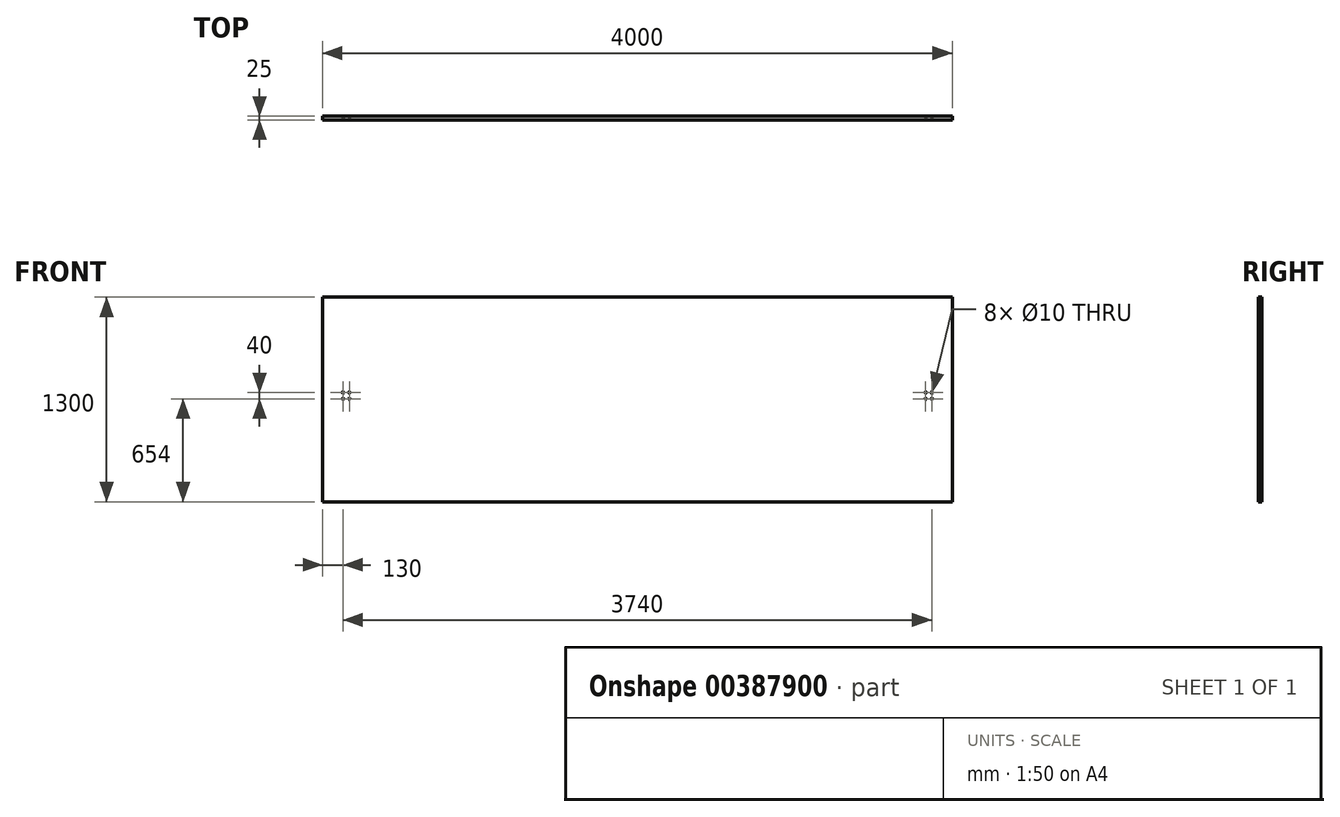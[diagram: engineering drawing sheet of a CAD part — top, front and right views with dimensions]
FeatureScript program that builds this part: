
annotation { "Feature Type Name" : "Feature", "Feature Type Description" : "" }
export const myFeature = defineFeature(function(context is Context, id is Id, definition is map)
    precondition{}
    {
        {
            var Q0;
            Q0=qCreatedBy(makeId("Front.planeOp"),FACE);
            var sketch = newSketch(context, id + "F0", { "sketchPlane" : qUnion([Q0])});
            skLineSegment(sketch, "E0.bottom", {"start": v(-2000, 650) * mm, "end": v(2000, 650) * mm});
            skLineSegment(sketch, "E0.top", {"start": v(-2000, -650) * mm, "end": v(2000, -650) * mm});
            skLineSegment(sketch, "E0.left", {"start": v(-2000, 650) * mm, "end": v(-2000, -650) * mm});
            skLineSegment(sketch, "E0.right", {"start": v(2000, 650) * mm, "end": v(2000, -650) * mm});
            skPoint(sketch, "E0.middle", {"position": v(0, 0) * mm});
            skSolve(sketch);
        }
        {
            var Q0;
            Q0 = qSketchRegion(id + "F0", true);
            extrude(context, id + "F1", {"entities" : qUnion([Q0]), "depth" : 25 * mm});
        }
        {
            var Q0;
            Q0=makeQuery(id+"F1.opExtrude","CAP_FACE",FACE,{"disambiguationData":[OSD([sQuery(id+"F0.wireOp",EDGE,"E0.bottom"),sQuery(id+"F0.wireOp",EDGE,"E0.top"),sQuery(id+"F0.wireOp",EDGE,"E0.left"),sQuery(id+"F0.wireOp",EDGE,"E0.right")])],"isStart":false});
            var sketch = newSketch(context, id + "F2", { "sketchPlane" : qUnion([Q0])});
            skLineSegment(sketch, "E1", {"start": v(-2000, 650) * mm, "end": v(-1850, 650) * mm});
            skLineSegment(sketch, "E2", {"start": v(-1850, 650) * mm, "end": v(-1850, 24) * mm});
            skLineSegment(sketch, "E3.bottom", {"start": v(-1870, 44) * mm, "end": v(-1830, 44) * mm});
            skLineSegment(sketch, "E3.top", {"start": v(-1870, 4) * mm, "end": v(-1830, 4) * mm});
            skLineSegment(sketch, "E3.left", {"start": v(-1870, 44) * mm, "end": v(-1870, 4) * mm});
            skLineSegment(sketch, "E3.right", {"start": v(-1830, 44) * mm, "end": v(-1830, 4) * mm});
            skPoint(sketch, "E3.middle", {"position": v(-1850, 24) * mm});
            skLineSegment(sketch, "E4", {"start": v(2000, 650) * mm, "end": v(1850, 650) * mm});
            skLineSegment(sketch, "E5", {"start": v(1850, 650) * mm, "end": v(1850, 24) * mm});
            skLineSegment(sketch, "E6.bottom", {"start": v(1830, 44) * mm, "end": v(1870, 44) * mm});
            skLineSegment(sketch, "E6.top", {"start": v(1830, 4) * mm, "end": v(1870, 4) * mm});
            skLineSegment(sketch, "E6.left", {"start": v(1830, 44) * mm, "end": v(1830, 4) * mm});
            skLineSegment(sketch, "E6.right", {"start": v(1870, 44) * mm, "end": v(1870, 4) * mm});
            skPoint(sketch, "E6.middle", {"position": v(1850, 24) * mm});
            skSolve(sketch);
        }
        {
            var Q0;
            Q0=sQuery(id+"F2.wireOp",VERTEX,"E3.bottom.start");
            var Q1;
            Q1=sQuery(id+"F2.wireOp",VERTEX,"E3.bottom.end");
            var Q2;
            Q2=sQuery(id+"F2.wireOp",VERTEX,"E3.right.end");
            var Q3;
            Q3=sQuery(id+"F2.wireOp",VERTEX,"E3.top.start");
            var Q4;
            Q4=makeQuery(id+"F1.opExtrude","SWEPT_BODY",BODY,{"disambiguationData":[OSD([sQuery(id+"F0.wireOp",EDGE,"E0.bottom"),sQuery(id+"F0.wireOp",EDGE,"E0.top"),sQuery(id+"F0.wireOp",EDGE,"E0.left"),sQuery(id+"F0.wireOp",EDGE,"E0.right")])]});
            hole(context, id + "F3", {"style" : HoleStyle.SIMPLE, "endStyle" : HoleEndStyle.THROUGH, "holeDiameter" : 10 * mm, "isTappedThrough" : true, "tappedDepth" : 12 * mm, "tapClearance" : 3, "locations" : qUnion([Q0, Q1, Q2, Q3]), "scope" : qUnion([Q4])});
        }
        {
            var Q0;
            Q0=sQuery(id+"F2.wireOp",VERTEX,"E6.bottom.start");
            var Q1;
            Q1=sQuery(id+"F2.wireOp",VERTEX,"E6.bottom.end");
            var Q2;
            Q2=sQuery(id+"F2.wireOp",VERTEX,"E6.top.end");
            var Q3;
            Q3=sQuery(id+"F2.wireOp",VERTEX,"E6.top.start");
            var Q4;
            Q4=makeQuery(id+"F1.opExtrude","SWEPT_BODY",BODY,{"disambiguationData":[OSD([sQuery(id+"F0.wireOp",EDGE,"E0.bottom"),sQuery(id+"F0.wireOp",EDGE,"E0.top"),sQuery(id+"F0.wireOp",EDGE,"E0.left"),sQuery(id+"F0.wireOp",EDGE,"E0.right")])]});
            hole(context, id + "F4", {"style" : HoleStyle.SIMPLE, "endStyle" : HoleEndStyle.THROUGH, "holeDiameter" : 10 * mm, "isTappedThrough" : true, "tappedDepth" : 12 * mm, "tapClearance" : 3, "locations" : qUnion([Q0, Q1, Q2, Q3]), "scope" : qUnion([Q4])});
        }
    });
